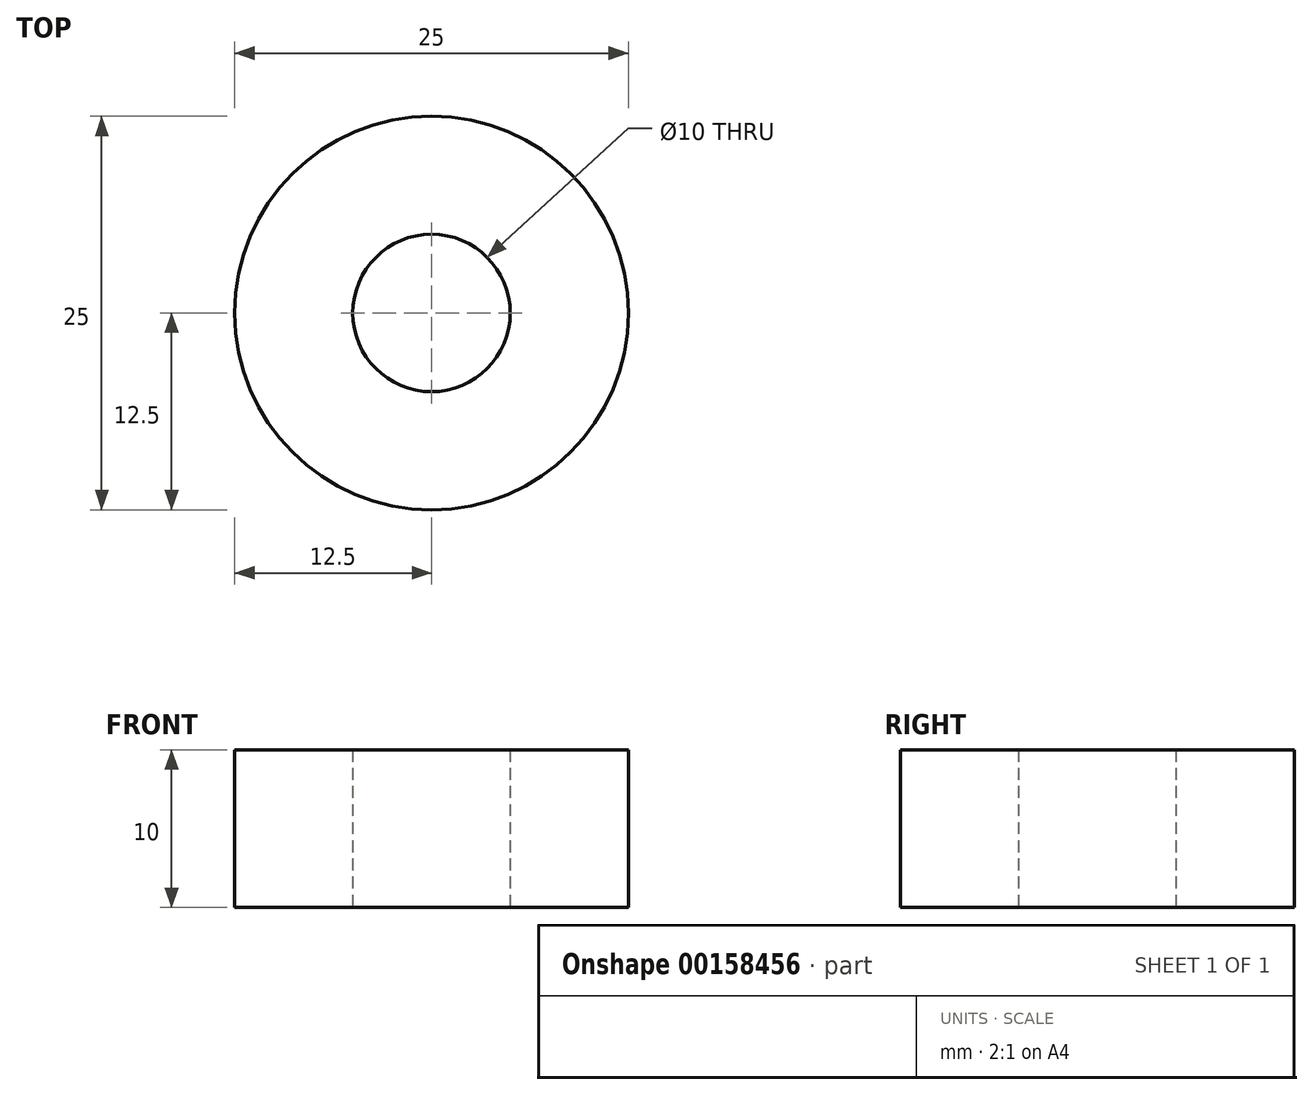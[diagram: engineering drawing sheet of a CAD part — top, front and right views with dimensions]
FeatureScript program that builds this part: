
annotation { "Feature Type Name" : "Feature", "Feature Type Description" : "" }
export const myFeature = defineFeature(function(context is Context, id is Id, definition is map)
    precondition{}
    {
        {
            var Q0;
            Q0=qCreatedBy(makeId("Top.planeOp"),FACE);
            var sketch = newSketch(context, id + "F0", { "sketchPlane" : qUnion([Q0])});
            skCircle(sketch, "E0", {"center": v(0, 0) * mm, "radius": 12.5 * mm});
            skCircle(sketch, "E1", {"center": v(0, 0) * mm, "radius": 5 * mm});
            skSolve(sketch);
        }
        {
            var Q0;
            Q0 = qSketchRegion(id + "F0", true);
            var Q1;
            Q1=makeQuery(id+"F0.imprint","IMPRINT",FACE,{"disambiguationData":[TD([[makeQuery(id+"F0.imprint","IMPRINT",EDGE,{"derivedFrom":sQuery(id+"F0.wireOp",EDGE,"E0")}),1.0]])]});
            extrude(context, id + "F1", {"entities" : qUnion([Q0, Q1]), "depth" : 10 * mm});
        }
    });
